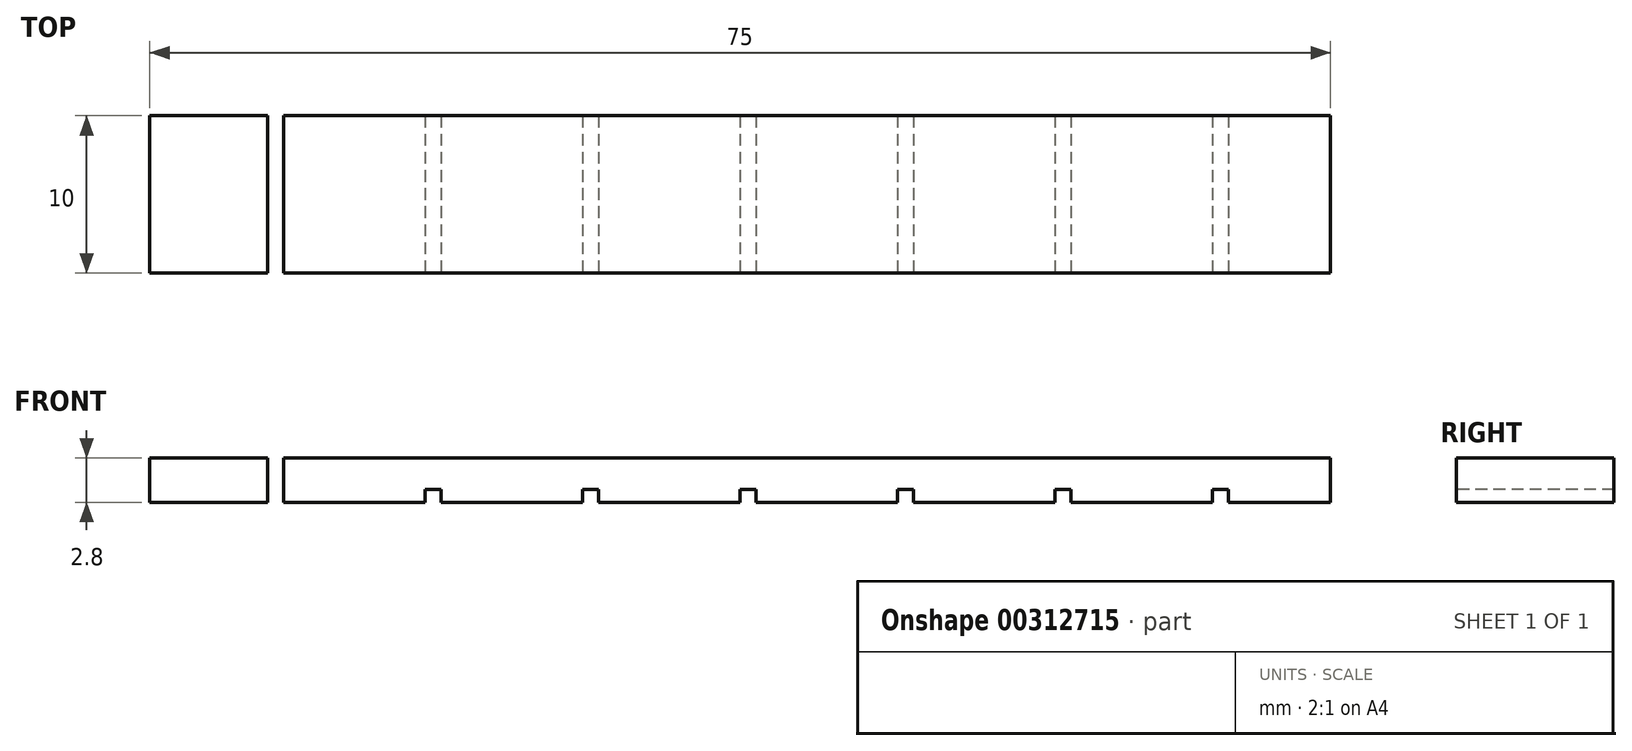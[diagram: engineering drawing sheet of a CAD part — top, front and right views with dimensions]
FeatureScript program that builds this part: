
annotation { "Feature Type Name" : "Feature", "Feature Type Description" : "" }
export const myFeature = defineFeature(function(context is Context, id is Id, definition is map)
    precondition{}
    {
        {
            var Q0;
            Q0=qCreatedBy(makeId("Top.planeOp"),FACE);
            var sketch = newSketch(context, id + "F0", { "sketchPlane" : qUnion([Q0])});
            skLineSegment(sketch, "E0.bottom", {"start": v(37.5, -5) * mm, "end": v(-37.5, -5) * mm});
            skLineSegment(sketch, "E0.top", {"start": v(37.5, 5) * mm, "end": v(-37.5, 5) * mm});
            skLineSegment(sketch, "E0.left", {"start": v(37.5, -5) * mm, "end": v(37.5, 5) * mm});
            skLineSegment(sketch, "E0.right", {"start": v(-37.5, -5) * mm, "end": v(-37.5, 5) * mm});
            skPoint(sketch, "E0.middle", {"position": v(0, 0) * mm});
            skLineSegment(sketch, "E1.bottom", {"start": v(-30, 5) * mm, "end": v(-29, 5) * mm});
            skLineSegment(sketch, "E1.top", {"start": v(-30, -5) * mm, "end": v(-29, -5) * mm});
            skLineSegment(sketch, "E1.left", {"start": v(-30, 5) * mm, "end": v(-30, -5) * mm});
            skLineSegment(sketch, "E1.right", {"start": v(-29, 5) * mm, "end": v(-29, -5) * mm});
            skLineSegment(sketch, "E2.1.0.0", {"start": v(-19, 5) * mm, "end": v(-19, -5) * mm});
            skLineSegment(sketch, "E2.1.0.1", {"start": v(-20, 5) * mm, "end": v(-20, -5) * mm});
            skLineSegment(sketch, "E2.2.0.0", {"start": v(-9, 5) * mm, "end": v(-9, -5) * mm});
            skLineSegment(sketch, "E2.2.0.1", {"start": v(-10, 5) * mm, "end": v(-10, -5) * mm});
            skLineSegment(sketch, "E2.3.0.0", {"start": v(1, 5) * mm, "end": v(1, -5) * mm});
            skLineSegment(sketch, "E2.3.0.1", {"start": v(0, 5) * mm, "end": v(0, -5) * mm});
            skLineSegment(sketch, "E2.4.0.0", {"start": v(11, 5) * mm, "end": v(11, -5) * mm});
            skLineSegment(sketch, "E2.4.0.1", {"start": v(10, 5) * mm, "end": v(10, -5) * mm});
            skLineSegment(sketch, "E2.5.0.0", {"start": v(21, 5) * mm, "end": v(21, -5) * mm});
            skLineSegment(sketch, "E2.5.0.1", {"start": v(20, 5) * mm, "end": v(20, -5) * mm});
            skLineSegment(sketch, "E2.6.0.0", {"start": v(31, 5) * mm, "end": v(31, -5) * mm});
            skLineSegment(sketch, "E2.6.0.1", {"start": v(30, 5) * mm, "end": v(30, -5) * mm});
            skLineSegment(sketch, "E2.direction1", {"start": v(-29, -5) * mm, "end": v(-19, -5) * mm, "construction": true});
            skSolve(sketch);
        }
        {
            var Q0;
            {var subQ0=sQuery(id+"F0.wireOp",EDGE,"E1.right");Q0=makeQuery(id+"F0.imprint","IMPRINT",FACE,{"disambiguationData":[TD([[makeQuery(id+"F0.imprint","IMPRINT",EDGE,{"derivedFrom":subQ0}),1.0]])]});}
            var Q1;
            Q1=makeQuery(id+"F0.imprint","IMPRINT",FACE,{"disambiguationData":[TD([[makeQuery(id+"F0.imprint","IMPRINT",EDGE,{"derivedFrom":sQuery(id+"F0.wireOp",EDGE,"E1.bottom")}),-1.0]])]});
            var Q2;
            {var subQ0=sQuery(id+"F0.wireOp",EDGE,"E0.left");Q2=makeQuery(id+"F0.imprint","IMPRINT",FACE,{"disambiguationData":[TD([[makeQuery(id+"F0.imprint","IMPRINT",EDGE,{"derivedFrom":subQ0}),1.0]])]});}
            var Q3;
            {var subQ0=sQuery(id+"F0.wireOp",EDGE,"E0.right");Q3=makeQuery(id+"F0.imprint","IMPRINT",FACE,{"disambiguationData":[TD([[makeQuery(id+"F0.imprint","IMPRINT",EDGE,{"derivedFrom":subQ0}),-1.0]])]});}
            var Q4;
            {var subQ0=sQuery(id+"F0.wireOp",EDGE,"E2.6.0.0");Q4=makeQuery(id+"F0.imprint","IMPRINT",FACE,{"disambiguationData":[TD([[makeQuery(id+"F0.imprint","IMPRINT",EDGE,{"derivedFrom":subQ0}),-1.0]])]});}
            var Q5;
            {var subQ0=sQuery(id+"F0.wireOp",EDGE,"E2.5.0.0");Q5=makeQuery(id+"F0.imprint","IMPRINT",FACE,{"disambiguationData":[TD([[makeQuery(id+"F0.imprint","IMPRINT",EDGE,{"derivedFrom":subQ0}),1.0]])]});}
            var Q6;
            {var subQ0=sQuery(id+"F0.wireOp",EDGE,"E2.5.0.0");Q6=makeQuery(id+"F0.imprint","IMPRINT",FACE,{"disambiguationData":[TD([[makeQuery(id+"F0.imprint","IMPRINT",EDGE,{"derivedFrom":subQ0}),-1.0]])]});}
            var Q7;
            {var subQ0=sQuery(id+"F0.wireOp",EDGE,"E2.4.0.0");Q7=makeQuery(id+"F0.imprint","IMPRINT",FACE,{"disambiguationData":[TD([[makeQuery(id+"F0.imprint","IMPRINT",EDGE,{"derivedFrom":subQ0}),1.0]])]});}
            var Q8;
            {var subQ0=sQuery(id+"F0.wireOp",EDGE,"E2.4.0.0");Q8=makeQuery(id+"F0.imprint","IMPRINT",FACE,{"disambiguationData":[TD([[makeQuery(id+"F0.imprint","IMPRINT",EDGE,{"derivedFrom":subQ0}),-1.0]])]});}
            var Q9;
            {var subQ0=sQuery(id+"F0.wireOp",EDGE,"E2.3.0.0");Q9=makeQuery(id+"F0.imprint","IMPRINT",FACE,{"disambiguationData":[TD([[makeQuery(id+"F0.imprint","IMPRINT",EDGE,{"derivedFrom":subQ0}),1.0]])]});}
            var Q10;
            {var subQ0=sQuery(id+"F0.wireOp",EDGE,"E2.3.0.0");Q10=makeQuery(id+"F0.imprint","IMPRINT",FACE,{"disambiguationData":[TD([[makeQuery(id+"F0.imprint","IMPRINT",EDGE,{"derivedFrom":subQ0}),-1.0]])]});}
            var Q11;
            {var subQ0=sQuery(id+"F0.wireOp",EDGE,"E2.2.0.0");Q11=makeQuery(id+"F0.imprint","IMPRINT",FACE,{"disambiguationData":[TD([[makeQuery(id+"F0.imprint","IMPRINT",EDGE,{"derivedFrom":subQ0}),1.0]])]});}
            var Q12;
            {var subQ0=sQuery(id+"F0.wireOp",EDGE,"E2.2.0.0");Q12=makeQuery(id+"F0.imprint","IMPRINT",FACE,{"disambiguationData":[TD([[makeQuery(id+"F0.imprint","IMPRINT",EDGE,{"derivedFrom":subQ0}),-1.0]])]});}
            var Q13;
            {var subQ0=sQuery(id+"F0.wireOp",EDGE,"E2.1.0.0");Q13=makeQuery(id+"F0.imprint","IMPRINT",FACE,{"disambiguationData":[TD([[makeQuery(id+"F0.imprint","IMPRINT",EDGE,{"derivedFrom":subQ0}),1.0]])]});}
            var Q14;
            {var subQ0=sQuery(id+"F0.wireOp",EDGE,"E2.1.0.0");Q14=makeQuery(id+"F0.imprint","IMPRINT",FACE,{"disambiguationData":[TD([[makeQuery(id+"F0.imprint","IMPRINT",EDGE,{"derivedFrom":subQ0}),-1.0]])]});}
            extrude(context, id + "F1", {"entities" : qUnion([Q0, Q1, Q2, Q3, Q4, Q5, Q6, Q7, Q8, Q9, Q10, Q11, Q12, Q13, Q14]), "depth" : 2.8 * mm});
        }
        {
            var Q0;
            Q0=makeQuery(id+"F0.imprint","IMPRINT",FACE,{"disambiguationData":[TD([[makeQuery(id+"F0.imprint","IMPRINT",EDGE,{"derivedFrom":sQuery(id+"F0.wireOp",EDGE,"E1.bottom")}),-1.0]])]});
            var Q1;
            {var subQ0=sQuery(id+"F0.wireOp",EDGE,"E2.1.0.0");Q1=makeQuery(id+"F0.imprint","IMPRINT",FACE,{"disambiguationData":[TD([[makeQuery(id+"F0.imprint","IMPRINT",EDGE,{"derivedFrom":subQ0}),-1.0]])]});}
            var Q2;
            {var subQ0=sQuery(id+"F0.wireOp",EDGE,"E2.2.0.0");Q2=makeQuery(id+"F0.imprint","IMPRINT",FACE,{"disambiguationData":[TD([[makeQuery(id+"F0.imprint","IMPRINT",EDGE,{"derivedFrom":subQ0}),-1.0]])]});}
            var Q3;
            {var subQ0=sQuery(id+"F0.wireOp",EDGE,"E2.3.0.0");Q3=makeQuery(id+"F0.imprint","IMPRINT",FACE,{"disambiguationData":[TD([[makeQuery(id+"F0.imprint","IMPRINT",EDGE,{"derivedFrom":subQ0}),-1.0]])]});}
            var Q4;
            {var subQ0=sQuery(id+"F0.wireOp",EDGE,"E2.4.0.0");Q4=makeQuery(id+"F0.imprint","IMPRINT",FACE,{"disambiguationData":[TD([[makeQuery(id+"F0.imprint","IMPRINT",EDGE,{"derivedFrom":subQ0}),-1.0]])]});}
            var Q5;
            {var subQ0=sQuery(id+"F0.wireOp",EDGE,"E2.5.0.0");Q5=makeQuery(id+"F0.imprint","IMPRINT",FACE,{"disambiguationData":[TD([[makeQuery(id+"F0.imprint","IMPRINT",EDGE,{"derivedFrom":subQ0}),-1.0]])]});}
            var Q6;
            {var subQ0=sQuery(id+"F0.wireOp",EDGE,"E2.6.0.0");Q6=makeQuery(id+"F0.imprint","IMPRINT",FACE,{"disambiguationData":[TD([[makeQuery(id+"F0.imprint","IMPRINT",EDGE,{"derivedFrom":subQ0}),-1.0]])]});}
            extrude(context, id + "F2", {"entities" : qUnion([Q0, Q1, Q2, Q3, Q4, Q5, Q6]), "operationType" : NewBodyOperationType.REMOVE, "depth" : 0.8 * mm});
        }
    });
